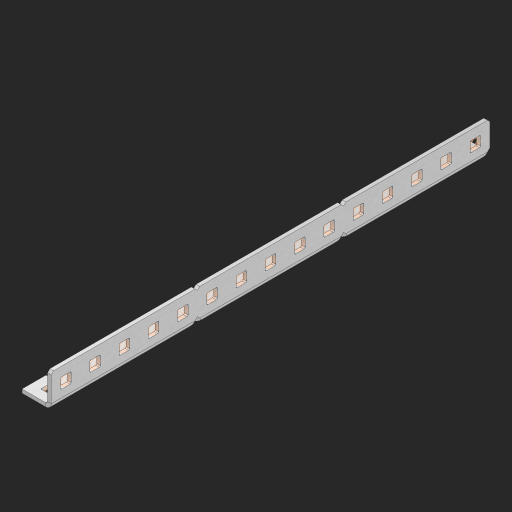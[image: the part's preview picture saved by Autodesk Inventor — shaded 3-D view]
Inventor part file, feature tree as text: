
AUTODESK INVENTOR PART (.ipt)
format: ipt  version: 2023 (Build 270158000, 158)  size: 857,600 bytes
history: native  units: in
note: dims shown in document units (in); Inventor stores cm internally (conversion verified against a paired STEP export)
features: other x193, extrude x43, sheet_metal_op x11, sketch x10, pattern_linear x2, mirror x1, chamfer x1
ambient origin geometry x8: Origin, YZ Plane, XZ Plane, XY Plane, X Axis, Y Axis, Z Axis, Center Point
bodies: Solid1 (feature_tree), Body (feature_tree)
feature tree (261):
  other  "Alu Half C 1x2x1x15"
  other  "Table"
  other  "Alu C 1x2x1x35"
  other  "Alu C 1x2x1x34"
  other  "Alu C 1x2x1x33"
  other  "Alu C 1x2x1x32"
  other  "Alu C 1x2x1x31"
  other  "Alu C 1x2x1x30"
  other  "Alu C 1x2x1x29"
  other  "Alu C 1x2x1x28"
  other  "Alu C 1x2x1x27"
  other  "Alu C 1x2x1x26"
  other  "Alu C 1x2x1x25"
  other  "Alu C 1x2x1x24"
  other  "Alu C 1x2x1x23"
  other  "Alu C 1x2x1x22"
  other  "Alu C 1x2x1x21"
  other  "Alu C 1x2x1x20"
  other  "Alu C 1x2x1x19"
  other  "Alu C 1x2x1x18"
  other  "Alu C 1x2x1x17"
  other  "Alu C 1x2x1x16"
  other  "Alu C 1x2x1x15"
  other  "Alu C 1x2x1x14"
  other  "Alu C 1x2x1x13"
  other  "Alu C 1x2x1x12"
  other  "Alu C 1x2x1x11"
  other  "Alu C 1x2x1x10"
  other  "Alu C 1x2x1x9"
  other  "Alu C 1x2x1x8"
  other  "Alu C 1x2x1x7"
  other  "Alu C 1x2x1x6"
  other  "Alu C 1x2x1x5"
  other  "Alu C 1x2x1x4"
  other  "Alu C 1x2x1x3"
  other  "Alu C 1x2x1x2"
  other  "Alu C 1x2x1x1"
  other  "Steel C 1x2x1x35"
  other  "Steel C 1x2x1x34"
  other  "Steel C 1x2x1x33"
  other  "Steel C 1x2x1x32"
  other  "Steel C 1x2x1x31"
  other  "Steel C 1x2x1x30"
  other  "Steel C 1x2x1x29"
  other  "Steel C 1x2x1x28"
  other  "Steel C 1x2x1x27"
  other  "Steel C 1x2x1x26"
  other  "Steel C 1x2x1x25"
  other  "Steel C 1x2x1x24"
  other  "Steel C 1x2x1x23"
  other  "Steel C 1x2x1x22"
  other  "Steel C 1x2x1x21"
  other  "Steel C 1x2x1x20"
  other  "Steel C 1x2x1x19"
  other  "Steel C 1x2x1x18"
  other  "Steel C 1x2x1x17"
  other  "Steel C 1x2x1x16"
  other  "Steel C 1x2x1x15"
  other  "Steel C 1x2x1x14"
  other  "Steel C 1x2x1x13"
  other  "Steel C 1x2x1x12"
  other  "Steel C 1x2x1x11"
  other  "Steel C 1x2x1x10"
  other  "Steel C 1x2x1x9"
  other  "Steel C 1x2x1x8"
  other  "Steel C 1x2x1x7"
  other  "Steel C 1x2x1x6"
  other  "Steel C 1x2x1x5"
  other  "Steel C 1x2x1x4"
  other  "Steel C 1x2x1x3"
  other  "Steel C 1x2x1x2"
  other  "Steel C 1x2x1x1"
  other  "Alu Half C 1x2x1x35"
  other  "Alu Half C 1x2x1x34"
  other  "Alu Half C 1x2x1x33"
  other  "Alu Half C 1x2x1x32"
  other  "Alu Half C 1x2x1x31"
  other  "Alu Half C 1x2x1x30"
  other  "Alu Half C 1x2x1x29"
  other  "Alu Half C 1x2x1x28"
  other  "Alu Half C 1x2x1x27"
  other  "Alu Half C 1x2x1x26"
  other  "Alu Half C 1x2x1x25"
  other  "Alu Half C 1x2x1x24"
  other  "Alu Half C 1x2x1x23"
  other  "Alu Half C 1x2x1x22"
  other  "Alu Half C 1x2x1x21"
  other  "Alu Half C 1x2x1x20"
  other  "Alu Half C 1x2x1x19"
  other  "Alu Half C 1x2x1x18"
  other  "Alu Half C 1x2x1x17"
  other  "Alu Half C 1x2x1x16"
  other  "Alu Half C 1x2x1x14"
  other  "Alu Half C 1x2x1x13"
  other  "Alu Half C 1x2x1x12"
  other  "Alu Half C 1x2x1x11"
  other  "Alu Half C 1x2x1x10"
  other  "Alu Half C 1x2x1x9"
  other  "Alu Half C 1x2x1x8"
  other  "Alu Half C 1x2x1x7"
  other  "Alu Half C 1x2x1x6"
  other  "Alu Half C 1x2x1x5"
  other  "Alu Half C 1x2x1x4"
  other  "Alu Half C 1x2x1x3"
  other  "Alu Half C 1x2x1x2"
  other  "Alu Half C 1x2x1x1"
  other  "Steel Half C 1x2x1x35"
  other  "Steel Half C 1x2x1x34"
  other  "Steel Half C 1x2x1x33"
  other  "Steel Half C 1x2x1x32"
  other  "Steel Half C 1x2x1x31"
  other  "Steel Half C 1x2x1x30"
  other  "Steel Half C 1x2x1x29"
  other  "Steel Half C 1x2x1x28"
  other  "Steel Half C 1x2x1x27"
  other  "Steel Half C 1x2x1x26"
  other  "Steel Half C 1x2x1x25"
  other  "Steel Half C 1x2x1x24"
  other  "Steel Half C 1x2x1x23"
  other  "Steel Half C 1x2x1x22"
  other  "Steel Half C 1x2x1x21"
  other  "Steel Half C 1x2x1x20"
  other  "Steel Half C 1x2x1x19"
  other  "Steel Half C 1x2x1x18"
  other  "Steel Half C 1x2x1x17"
  other  "Steel Half C 1x2x1x16"
  other  "Steel Half C 1x2x1x15"
  other  "Steel Half C 1x2x1x14"
  other  "Steel Half C 1x2x1x13"
  other  "Steel Half C 1x2x1x12"
  other  "Steel Half C 1x2x1x11"
  other  "Steel Half C 1x2x1x10"
  other  "Steel Half C 1x2x1x9"
  other  "Steel Half C 1x2x1x8"
  other  "Steel Half C 1x2x1x7"
  other  "Steel Half C 1x2x1x6"
  other  "Steel Half C 1x2x1x5"
  other  "Steel Half C 1x2x1x4"
  other  "Steel Half C 1x2x1x3"
  other  "Steel Half C 1x2x1x2"
  other  "Steel Half C 1x2x1x1"
  sheet_metal_op  "Flanges"
  other  "Flange Pattern Plane"
  other  "Flange Pattern Sketch"
  sheet_metal_op  "Flange Pattern"
  sheet_metal_op  "Body Pattern"
  pattern_linear  "Center Pattern"  Spacing1=0.0625in  [1 undecoded]
  other  "Arc Length"
  mirror  "Notch Mirror"
  pattern_linear  "Notch Pattern"  Spacing1=0.182in  [1 undecoded]
  chamfer  "End Chamfer"
  extrude  "Half Cut"  Depth=0.02in
  sketch  "Sketch1"  dims[d0=1.0in]
  other  "Plate1"
  sketch  "Sketch2"  dims[d1=7.5in]
  other  "Plate2"
  sheet_metal_op  "Bend1"
  sheet_metal_op  "Corner1"
  sketch  "Sketch3"  dims[d2=0.0625in]
  sketch  "Sketch7"  dims[d3=0.0625in]
  other  "Srf1"
  other  "Srf2"
  sketch  "Sketch8"  dims[d4=0.0312in]
  sketch  "Sketch9"  dims[d5=0.125in]
  other  "Srf91"
  sheet_metal_op  "Body Pattern Sketch"
  other  "Srf92"
  sketch  "Sketch13"  dims[d6=0.0625in]
  sketch  "Sketch14"  dims[d7=0.5in d8=90.0deg d9=0.0312in]
  sketch  "Sketch15"  dims[d10=0.25in]
  sketch  "Sketch16"  dims[d11=0.0625in d12=0.0625in d16=0.182in d17=0.02in d18=0.0625in d19=0.0in d20=0.25in d21=0.25in d38=5.9055in d40=0.5in d41=0.3937in d43=1.0in d46=0.172in d47=1.0in d48=0.0in d49=0.182in d50=0.02in d51=0.25in d52=0.25in d53=0.0625in d54=0.0in d55=0.172in d56=1.0in d57=0.0in d58=0.25in d60=5.9055in d62=0.5in d63=0.3937in d65=0.5in d85=0.1473in d86=0.1782in d88=0.04in d89=0.0625in d90=0.0in d91=0.04in d92=0.0491in d95=2.5in d96=0.04in d97=0.25in d98=45.0deg d99=0.25in d100=0.5in d101=0.0in d102=2.497in d106=0.182in d107=0.02in d108=0.5in d109=0.5in d110=0.0625in d111=0.0in d112=0.172in d113=0.5in d114=0.0in d117=0.5in d118=0.5in d119=0.5in]
  other  "Srf786"
  other  "Srf823"
  other  "Srf824"
  other  "Srf825"
  other  "Srf826"
  other  "Srf827"
  other  "Srf828"
  other  "Srf829"
  other  "Srf856"
  other  "Srf857"
  other  "Srf858"
  other  "Srf859"
  other  "Srf860"
  other  "Srf861"
  other  "Srf862"
  other  "Srf889"
  other  "Srf890"
  other  "Srf891"
  other  "Srf892"
  other  "Srf893"
  other  "Srf894"
  other  "Srf895"
  other  "Srf896"
  other  "Srf922"
  other  "Srf923"
  other  "Srf924"
  other  "Srf925"
  other  "Srf926"
  other  "Srf959"
  other  "Srf960"
  other  "Srf961"
  other  "Srf962"
  other  "Srf963"
  other  "Srf996"
  other  "Srf997"
  other  "Srf998"
  other  "Srf999"
  other  "Srf1000"
  other  "Srf1143"
  other  "Srf1199"
  other  "Srf1255"
  sheet_metal_op  "Flange Stamp"
  sheet_metal_op  "Flange Circle"
  sheet_metal_op  "Body Stamp"
  sheet_metal_op  "Body Circle"
  other  "Center Stamp"
  other  "Center Circle"
  sheet_metal_op  "Notch"
  extrude  "ExtrusionSrf2"  Depth=0.0625in
  extrude  "ExtrusionSrf92"  TaperAngle=0.0deg  [1 undecoded]
  extrude  "ExtrusionSrf823"  Depth=0.5in
  extrude  "ExtrusionSrf824"  Depth=0.5in
  extrude  "ExtrusionSrf825"  Depth=0.5in
  extrude  "ExtrusionSrf826"  Depth=0.5in
  extrude  "ExtrusionSrf827"  Depth=1.0in TaperAngle=0.0deg
  extrude  "ExtrusionSrf828"  Depth=0.182in
  extrude  "ExtrusionSrf829"  Depth=0.02in
  extrude  "ExtrusionSrf856"  Depth=0.5in
  extrude  "ExtrusionSrf857"  Depth=0.5in
  extrude  "ExtrusionSrf858"  Depth=0.0625in
  extrude  "ExtrusionSrf859"  TaperAngle=0.0deg  [1 undecoded]
  extrude  "ExtrusionSrf860"  Depth=0.5in
  extrude  "ExtrusionSrf861"  Depth=1.0in TaperAngle=0.0deg
  extrude  "ExtrusionSrf862"  Depth=0.5in
  extrude  "ExtrusionSrf889"  Depth=0.5in
  extrude  "ExtrusionSrf890"  Depth=0.5in
  extrude  "ExtrusionSrf891"  Depth=0.5in
  extrude  "ExtrusionSrf892"  Depth=0.5in
  extrude  "ExtrusionSrf893"  Depth=0.5in
  extrude  "ExtrusionSrf894"  Depth=0.0625in
  extrude  "ExtrusionSrf895"  TaperAngle=0.0deg  [1 undecoded]
  extrude  "ExtrusionSrf896"  Depth=0.5in
  extrude  "ExtrusionSrf922"  Depth=0.5in
  extrude  "ExtrusionSrf923"  Depth=2.5in
  extrude  "ExtrusionSrf924"  Depth=0.5in TaperAngle=45.0deg
  extrude  "ExtrusionSrf925"  Depth=0.5in
  extrude  "ExtrusionSrf926"  Depth=0.5in TaperAngle=0.0deg
  extrude  "ExtrusionSrf959"  Depth=0.5in
  extrude  "ExtrusionSrf960"  Depth=0.182in
  extrude  "ExtrusionSrf961"  Depth=0.02in
  extrude  "ExtrusionSrf962"  Depth=0.5in
  extrude  "ExtrusionSrf963"  Depth=0.5in
  extrude  "ExtrusionSrf996"  Depth=0.0625in
  extrude  "ExtrusionSrf997"  TaperAngle=0.0deg  [1 undecoded]
  extrude  "ExtrusionSrf998"  Depth=0.5in
  extrude  "ExtrusionSrf999"  Depth=0.5in TaperAngle=0.0deg
  extrude  "ExtrusionSrf1000"  Depth=0.5in
  extrude  "ExtrusionSrf1143"  Depth=0.5in
  extrude  "ExtrusionSrf1199"  Depth=0.5in
  extrude  "ExtrusionSrf1255"  [1 undecoded]
note: 7 required parameter values undecoded (feature->parameter linkage not recoverable at this tier; creation-order binding heuristic only, values carry confidence <= 0.55)
